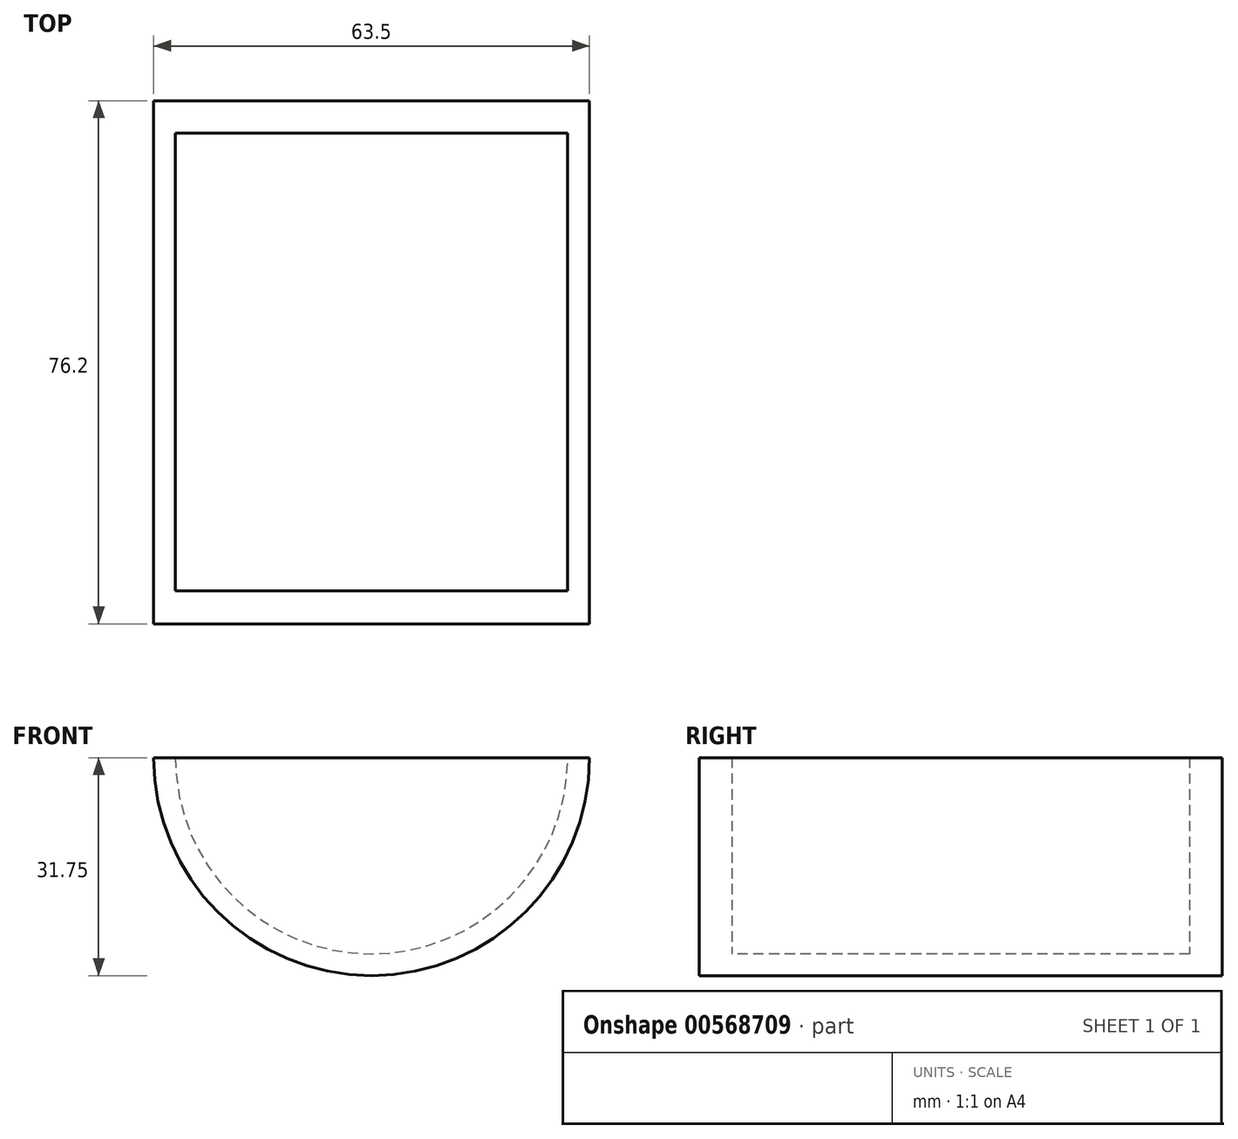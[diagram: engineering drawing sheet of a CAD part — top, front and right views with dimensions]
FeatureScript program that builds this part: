
annotation { "Feature Type Name" : "Feature", "Feature Type Description" : "" }
export const myFeature = defineFeature(function(context is Context, id is Id, definition is map)
    precondition{}
    {
        {
            var Q0;
            Q0=qCreatedBy(makeId("Front.planeOp"),FACE);
            var sketch = newSketch(context, id + "F0", { "sketchPlane" : qUnion([Q0])});
            skArc(sketch, "E0", {"start": v(-31.75, 0) * mm, "mid": v(0, -31.75) * mm, "end": v(31.75, 0) * mm});
            skLineSegment(sketch, "E1", {"start": v(0, 0) * mm, "end": v(31.75, 0) * mm});
            skLineSegment(sketch, "E2", {"start": v(0, 0) * mm, "end": v(-31.75, 0) * mm});
            skSolve(sketch);
        }
        {
            var Q0;
            Q0 = qSketchRegion(id + "F0", true);
            extrude(context, id + "F1", {"entities" : qUnion([Q0]), "endBound" : BoundingType.SYMMETRIC, "depth" : 76.2 * mm, "offsetDistance" : 25.4 * mm});
        }
        {
            var Q0;
            Q0=makeQuery(id+"F1.opExtrude","SWEPT_FACE",FACE,{"disambiguationData":[OSD([sQuery(id+"F0.wireOp",EDGE,"E1"),sQuery(id+"F0.wireOp",EDGE,"E2")])]});
            var sketch = newSketch(context, id + "F2", { "sketchPlane" : qUnion([Q0])});
            skLineSegment(sketch, "E3", {"start": v(28.57, 33.35) * mm, "end": v(28.58, -33.32) * mm});
            skLineSegment(sketch, "E4", {"start": v(28.58, -33.32) * mm, "end": v(0, -33.32) * mm});
            skLineSegment(sketch, "E5", {"start": v(0, -33.32) * mm, "end": v(0, 33.35) * mm});
            skLineSegment(sketch, "E6", {"start": v(0, 33.35) * mm, "end": v(28.57, 33.35) * mm});
            skLineSegment(sketch, "E7", {"start": v(0, -33.32) * mm, "end": v(0, -60.1) * mm});
            skPoint(sketch, "E7.endSnap0", {"position": v(0, -38.1) * mm});
            skSolve(sketch);
        }
        {
            var Q0;
            Q0 = qSketchRegion(id + "F2", true);
            var Q1;
            Q1=sQuery(id+"F2.wireOp",EDGE,"E7");
            revolve(context, id + "F3", {"operationType" : NewBodyOperationType.REMOVE, "entities" : qUnion([Q0]), "axis" : qUnion([Q1]), "revolveType" : RevolveType.FULL, "oppositeDirection" : true});
        }
    });
